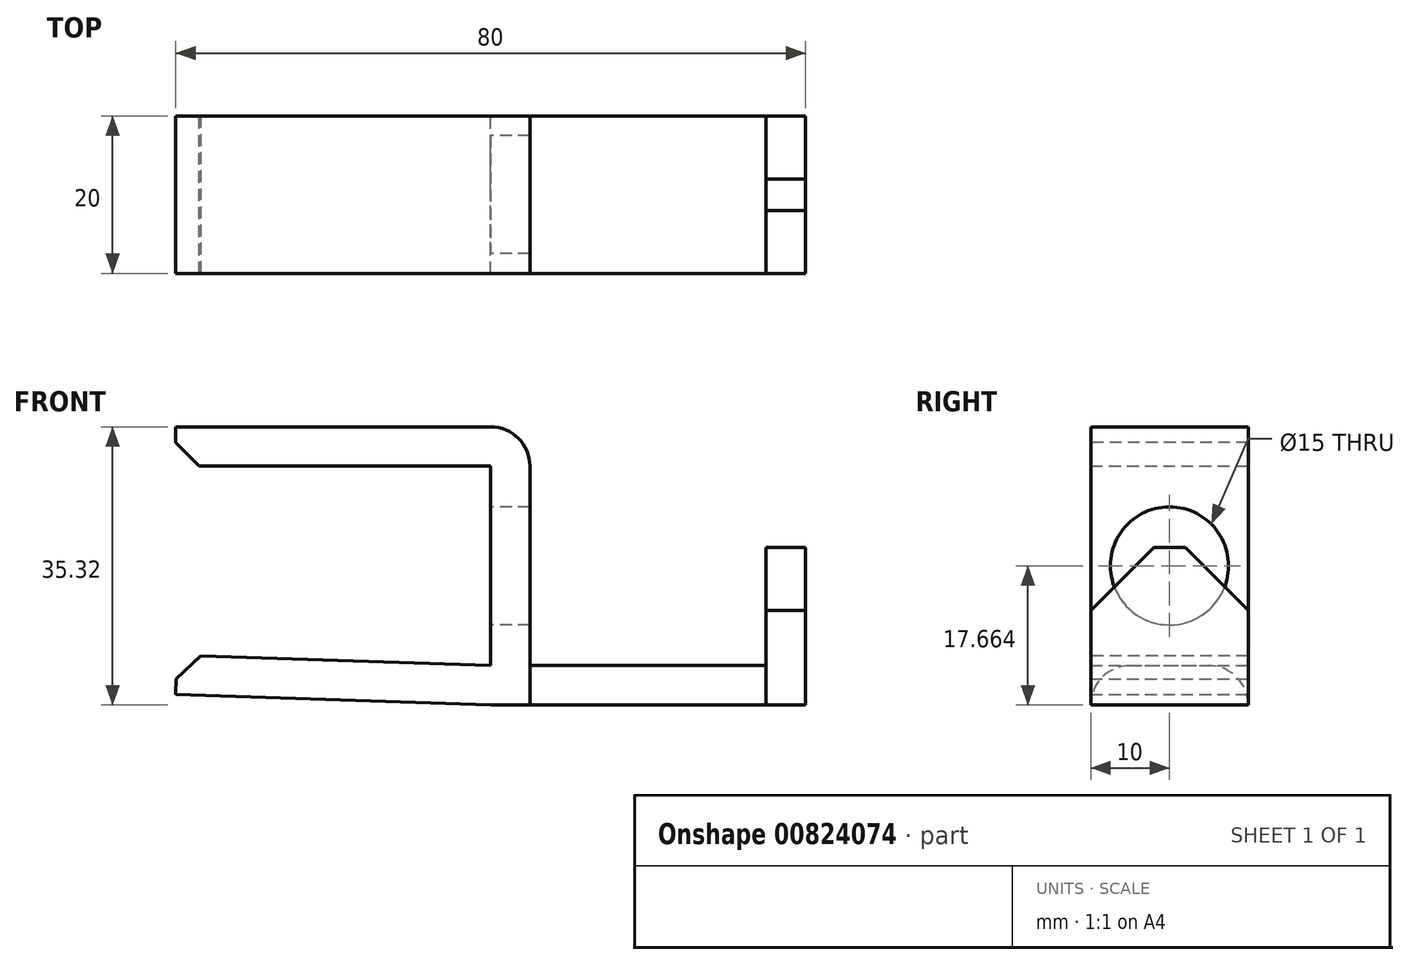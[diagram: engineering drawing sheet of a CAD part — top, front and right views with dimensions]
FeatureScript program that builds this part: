
annotation { "Feature Type Name" : "Feature", "Feature Type Description" : "" }
export const myFeature = defineFeature(function(context is Context, id is Id, definition is map)
    precondition{}
    {
        {
            var Q0;
            Q0=qCreatedBy(makeId("Front.planeOp"),FACE);
            var sketch = newSketch(context, id + "F0", { "sketchPlane" : qUnion([Q0])});
            skLineSegment(sketch, "E0.bottom", {"start": v(0, 52.94) * mm, "end": v(-40, 52.94) * mm});
            skLineSegment(sketch, "E0.top", {"start": v(0, 47.94) * mm, "end": v(-40, 47.94) * mm});
            skLineSegment(sketch, "E0.left", {"start": v(0, 52.94) * mm, "end": v(0, 47.94) * mm});
            skLineSegment(sketch, "E0.right", {"start": v(-40, 52.94) * mm, "end": v(-40, 47.94) * mm});
            skLineSegment(sketch, "E1.bottom", {"start": v(0, 52.94) * mm, "end": v(5, 52.94) * mm});
            skLineSegment(sketch, "E1.top", {"start": v(0, 17.62) * mm, "end": v(5, 17.62) * mm});
            skLineSegment(sketch, "E1.left", {"start": v(0, 52.94) * mm, "end": v(0, 17.62) * mm});
            skLineSegment(sketch, "E1.right", {"start": v(5, 52.94) * mm, "end": v(5, 17.62) * mm});
            skLineSegment(sketch, "E2.bottom", {"start": v(5, 17.62) * mm, "end": v(35, 17.62) * mm});
            skLineSegment(sketch, "E2.top", {"start": v(5, 22.62) * mm, "end": v(35, 22.62) * mm});
            skLineSegment(sketch, "E2.left", {"start": v(5, 17.62) * mm, "end": v(5, 22.62) * mm});
            skLineSegment(sketch, "E2.right", {"start": v(35, 17.62) * mm, "end": v(35, 22.62) * mm});
            skLineSegment(sketch, "E3.bottom", {"start": v(35, 17.62) * mm, "end": v(40, 17.62) * mm});
            skLineSegment(sketch, "E3.top", {"start": v(35, 37.62) * mm, "end": v(40, 37.62) * mm});
            skLineSegment(sketch, "E3.left", {"start": v(35, 17.62) * mm, "end": v(35, 37.62) * mm});
            skLineSegment(sketch, "E3.right", {"start": v(40, 17.62) * mm, "end": v(40, 37.62) * mm});
            skLineSegment(sketch, "E4", {"start": v(0, 17.62) * mm, "end": v(-40, 18.95) * mm});
            skLineSegment(sketch, "E5", {"start": v(-40, 18.95) * mm, "end": v(-39.83, 23.94) * mm});
            skLineSegment(sketch, "E6", {"start": v(-39.83, 23.94) * mm, "end": v(0, 22.62) * mm});
            skSolve(sketch);
        }
        {
            var Q0;
            Q0 = qSketchRegion(id + "F0", true);
            extrude(context, id + "F1", {"entities" : qUnion([Q0]), "depth" : 20 * mm, "offsetDistance" : 25 * mm});
        }
        {
            var Q0;
            Q0=makeQuery(id+"F1.opExtrude","CAP_EDGE",EDGE,{"disambiguationData":[OSD([sQuery(id+"F0.wireOp",EDGE,"E2.top")])],"isStart":false});
            var Q1;
            Q1=makeQuery(id+"F1.opExtrude","CAP_EDGE",EDGE,{"disambiguationData":[OSD([sQuery(id+"F0.wireOp",EDGE,"E2.top")])],"isStart":true});
            var Q2;
            Q2=makeQuery(id+"F1.opExtrude","SWEPT_EDGE",EDGE,{"disambiguationData":[OSD([sQuery(id+"F0.wireOp",EDGE,"E1.bottom"),sQuery(id+"F0.wireOp",EDGE,"E1.right")])]});
            fillet(context, id + "F2", {"entities" : qUnion([Q0, Q1, Q2]), "radius" : 5 * mm, "tangentPropagation" : true, "allowEdgeOverflow" : false});
        }
        {
            var Q0;
            Q0=makeQuery(id+"F1.opExtrude","SWEPT_EDGE",EDGE,{"disambiguationData":[OSD([sQuery(id+"F0.wireOp",EDGE,"E0.top"),sQuery(id+"F0.wireOp",EDGE,"E0.right")])]});
            var Q1;
            Q1=makeQuery(id+"F1.opExtrude","SWEPT_EDGE",EDGE,{"disambiguationData":[OSD([sQuery(id+"F0.wireOp",EDGE,"E5"),sQuery(id+"F0.wireOp",EDGE,"E6")])]});
            chamfer(context, id + "F3", {"entities" : qUnion([Q0, Q1]), "width" : 3 * mm, "tangentPropagation" : true});
        }
        {
            var Q0;
            Q0=makeQuery(id+"F1.opExtrude","SWEPT_FACE",FACE,{"disambiguationData":[OSD([sQuery(id+"F0.wireOp",EDGE,"E1.left")])]});
            var sketch = newSketch(context, id + "F4", { "sketchPlane" : qUnion([Q0])});
            skPoint(sketch, "E7", {"position": v(10, 35.28) * mm});
            skPoint(sketch, "E7.positionSnap0", {"position": v(0, 35.28) * mm});
            skPoint(sketch, "E7.positionSnap1", {"position": v(10, 47.94) * mm});
            skSolve(sketch);
        }
        {
            var Q0;
            Q0=sQuery(id+"F4.wireOp",VERTEX,"E7");
            var Q1;
            Q1=makeQuery(id+"F1.opExtrude","SWEPT_BODY",BODY,{"disambiguationData":[OSD([sQuery(id+"F0.wireOp",EDGE,"E0.bottom"),sQuery(id+"F0.wireOp",EDGE,"E0.top"),sQuery(id+"F0.wireOp",EDGE,"E0.right"),sQuery(id+"F0.wireOp",EDGE,"E1.bottom"),sQuery(id+"F0.wireOp",EDGE,"E1.top"),sQuery(id+"F0.wireOp",EDGE,"E1.left"),sQuery(id+"F0.wireOp",EDGE,"E1.right"),sQuery(id+"F0.wireOp",EDGE,"E2.bottom"),sQuery(id+"F0.wireOp",EDGE,"E2.top"),sQuery(id+"F0.wireOp",EDGE,"E3.bottom"),sQuery(id+"F0.wireOp",EDGE,"E3.top"),sQuery(id+"F0.wireOp",EDGE,"E3.left"),sQuery(id+"F0.wireOp",EDGE,"E3.right"),sQuery(id+"F0.wireOp",EDGE,"E4"),sQuery(id+"F0.wireOp",EDGE,"E5"),sQuery(id+"F0.wireOp",EDGE,"E6")])]});
            hole(context, id + "F5", {"style" : HoleStyle.C_BORE, "endStyle" : HoleEndStyle.BLIND, "holeDiameter" : 15 * mm, "cBoreDiameter" : 15 * mm, "cBoreDepth" : 5 * mm, "majorDiameter" : 5 * mm, "holeDepth" : 20 * mm, "isTappedThrough" : true, "tappedDepth" : 12 * mm, "tapClearance" : 3, "locations" : qUnion([Q0]), "scope" : qUnion([Q1])});
        }
        {
            var Q0;
            Q0=makeQuery(id+"F1.opExtrude","CAP_EDGE",EDGE,{"disambiguationData":[OSD([sQuery(id+"F0.wireOp",EDGE,"E3.top")])],"isStart":true});
            var Q1;
            Q1=makeQuery(id+"F1.opExtrude","CAP_EDGE",EDGE,{"disambiguationData":[OSD([sQuery(id+"F0.wireOp",EDGE,"E3.top")])],"isStart":false});
            chamfer(context, id + "F6", {"entities" : qUnion([Q0, Q1]), "width" : 8 * mm, "tangentPropagation" : true});
        }
    });
